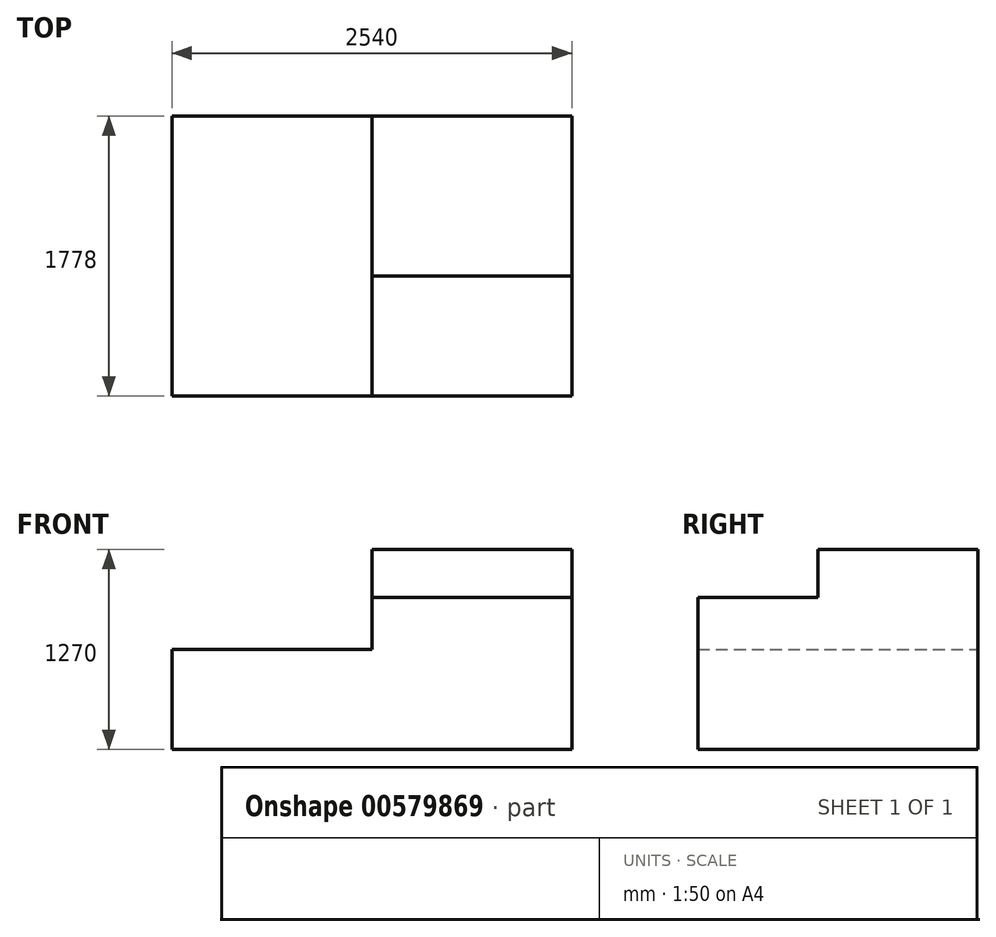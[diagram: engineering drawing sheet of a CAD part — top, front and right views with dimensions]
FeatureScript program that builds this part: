
annotation { "Feature Type Name" : "Feature", "Feature Type Description" : "" }
export const myFeature = defineFeature(function(context is Context, id is Id, definition is map)
    precondition{}
    {
        {
            var Q0;
            Q0=qCreatedBy(makeId("Front.planeOp"),FACE);
            var sketch = newSketch(context, id + "F0", { "sketchPlane" : qUnion([Q0])});
            skLineSegment(sketch, "E0", {"start": v(0, 0) * mm, "end": v(2540, 0) * mm});
            skLineSegment(sketch, "E1", {"start": v(0, 0) * mm, "end": v(0, 635) * mm});
            skLineSegment(sketch, "E2", {"start": v(0, 635) * mm, "end": v(1270, 635) * mm});
            skLineSegment(sketch, "E3", {"start": v(1270, 635) * mm, "end": v(1270, 965.2) * mm});
            skLineSegment(sketch, "E4", {"start": v(1270, 965.2) * mm, "end": v(2540, 965.2) * mm});
            skLineSegment(sketch, "E5", {"start": v(2540, 965.2) * mm, "end": v(2540, 0) * mm});
            skLineSegment(sketch, "E6", {"start": v(1270, 965.2) * mm, "end": v(1270, 1270) * mm});
            skLineSegment(sketch, "E7", {"start": v(1270, 1270) * mm, "end": v(2540, 1270) * mm});
            skLineSegment(sketch, "E8", {"start": v(2540, 1270) * mm, "end": v(2540, 965.2) * mm});
            skSolve(sketch);
        }
        {
            var Q0;
            Q0=makeQuery(id+"F0.imprint","IMPRINT",FACE,{"disambiguationData":[TD([[makeQuery(id+"F0.imprint","IMPRINT",EDGE,{"derivedFrom":sQuery(id+"F0.wireOp",EDGE,"E0")}),1.0]])]});
            var Q1;
            Q1=makeQuery(id+"F0.imprint","IMPRINT",FACE,{"disambiguationData":[TD([[makeQuery(id+"F0.imprint","IMPRINT",EDGE,{"derivedFrom":sQuery(id+"F0.wireOp",EDGE,"E4")}),1.0]])]});
            extrude(context, id + "F1", {"entities" : qUnion([Q0, Q1]), "depth" : 1778 * mm, "offsetDistance" : 25.4 * mm});
        }
        {
            var Q0;
            Q0=makeQuery(id+"F1.opExtrude","CAP_FACE",FACE,{"disambiguationData":[OSD([sQuery(id+"F0.wireOp",EDGE,"E0"),sQuery(id+"F0.wireOp",EDGE,"E1"),sQuery(id+"F0.wireOp",EDGE,"E2"),sQuery(id+"F0.wireOp",EDGE,"E3"),sQuery(id+"F0.wireOp",EDGE,"E5"),sQuery(id+"F0.wireOp",EDGE,"E6"),sQuery(id+"F0.wireOp",EDGE,"E7"),sQuery(id+"F0.wireOp",EDGE,"E8")])],"isStart":false});
            var sketch = newSketch(context, id + "F2", { "sketchPlane" : qUnion([Q0])});
            skLineSegment(sketch, "E9", {"start": v(1270, 965.2) * mm, "end": v(2540, 965.2) * mm});
            skSolve(sketch);
        }
        {
            var Q0;
            {var subQ0=sQuery(id+"F2.wireOp",EDGE,"E9");Q0=makeQuery(id+"F2.imprint","IMPRINT",FACE,{"disambiguationData":[TD([[makeQuery(id+"F2.imprint","IMPRINT",EDGE,{"derivedFrom":subQ0}),1.0]])]});}
            extrude(context, id + "F3", {"entities" : qUnion([Q0]), "operationType" : NewBodyOperationType.REMOVE, "oppositeDirection" : true, "depth" : 762 * mm, "offsetDistance" : 25.4 * mm});
        }
    });
